# Revit family: QF_GIORIK_GR0511M_GR0511L_GR0511E_GR0511P
name_source: partatom
category: Specialty Equipment
revit_build: Autodesk Revit 2014 (Build: 20140709_2115(x64)
units: mm (PartAtom-declared; Revit-internal decimal feet)

## types (4) — shared parameters
Assembly Code = E1090320
Cold Water Connection Height = 199 mm  [stored 0.652887 ft]
Cold Water Size = 1"
Cold Water Temperature Recommended = 0 °C
Cycle = 50 Hz
FL Amps = 0 A
HP = 0
Indirect Waste Connection Height = 46 mm  [stored 0.150919 ft]
Indirect Waste Flow = 0.0 L/s
Indirect Waste Size = 1"
Manufacturer = GIORIK
Min Ckt Ampacity = 0 A
URL = www.giorik.com
Waste Water Discharge Temperature = 0 °C
Weight in Pounds = 213.848

## per-type parameters (varying)
| type | Apparent Power | Description | Electronic control | Max Overcurrent Protection | Mechanical control | Phase | Programmable electronic control | Volts | Watts |
| GR0511M | 6300 VA | REGENERATING OVEN 5 GN 1/1 - MECHANICAL VERSION | No | 20 A | Yes | 3 | No | 400 V | 6300 W |
| GR0511P | 6300 VA | HOLDING CABINET-REGENERATOR 5 GN 1/1  - PROGRAMMABLE ELECTRONIC VERSION | No | 20 A | No | 3 | Yes | 400 V | 6300 W |
| GR0511E | 6300 VA | HOLDING CABINET-REGENERATOR 5 GN 1/1 - ELECTRONIC VERSION | Yes | 20 A | No | 3 | No | 400 V | 6300 W |
| GR0511L | 3300 VA | HOLDING CABINET-REGENERATOR 5 GN 1/1 – SINGLE-PHASE ELECTRONIC VERSION | Yes | 10 A | No | 1 | No | 230 V | 3300 W |

note: column(s) folded — value = type name in every type: Model

note: [stored X ft] marks values corroborated as IEEE doubles in the binary element streams (Revit-internal decimal feet)

## geometry (parser evidence)
native form markers: Blend x4, Sweep x3
no freeform markers — native parametric forms only
